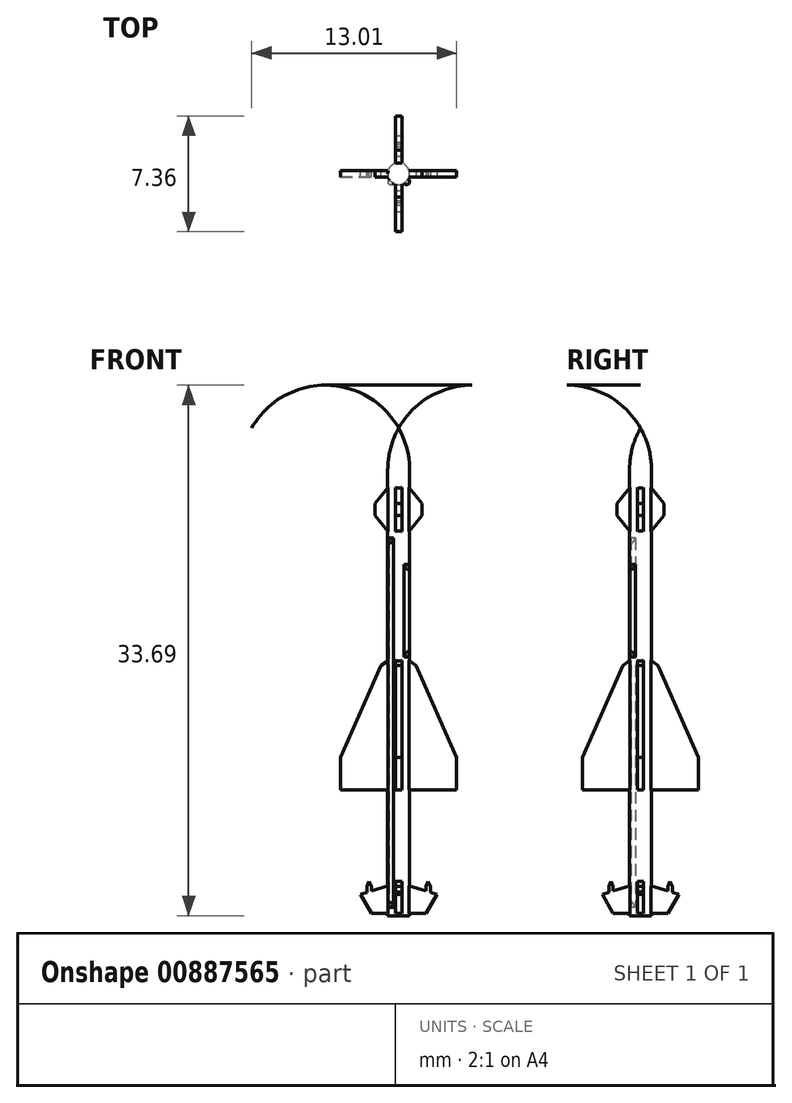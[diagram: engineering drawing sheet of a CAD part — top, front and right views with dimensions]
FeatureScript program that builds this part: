
annotation { "Feature Type Name" : "Feature", "Feature Type Description" : "" }
export const myFeature = defineFeature(function(context is Context, id is Id, definition is map)
    precondition{}
    {
        {
            var Q0;
            Q0=qCreatedBy(makeId("Front.planeOp"),FACE);
            var sketch = newSketch(context, id + "F0", { "sketchPlane" : qUnion([Q0])});
            skLineSegment(sketch, "E0", {"start": v(0, 0) * mm, "end": v(0, 30.97) * mm});
            skLineSegment(sketch, "E1", {"start": v(0.7, 28.33) * mm, "end": v(0.7, 0) * mm});
            skLineSegment(sketch, "E2", {"start": v(0.7, 0) * mm, "end": v(0, 0) * mm});
            skArc(sketch, "E3", {"start": v(0.7, 28.33) * mm, "mid": v(0.52, 29.7) * mm, "end": v(0, 30.97) * mm});
            skSolve(sketch);
        }
        {
            var Q0;
            Q0=makeQuery(id+"F0.imprint","IMPRINT",FACE,{"disambiguationData":[TD([[makeQuery(id+"F0.imprint","IMPRINT",EDGE,{"derivedFrom":sQuery(id+"F0.wireOp",EDGE,"E0")}),-1.0]])]});
            var Q1;
            Q1=sQuery(id+"F0.wireOp",EDGE,"E0");
            revolve(context, id + "F1", {"surfaceOperationType" : NewSurfaceOperationType.NEW, "entities" : qUnion([Q0]), "axis" : qUnion([Q1]), "revolveType" : RevolveType.FULL});
        }
        {
            var Q0;
            Q0=qCreatedBy(makeId("Front.planeOp"),FACE);
            var sketch = newSketch(context, id + "F2", { "sketchPlane" : qUnion([Q0])});
            skLineSegment(sketch, "E4.0", {"start": v(0.7, 28.33) * mm, "end": v(-0.7, 28.33) * mm, "construction": true});
            skLineSegment(sketch, "E5", {"start": v(0, 0.14) * mm, "end": v(1.74, 0.14) * mm});
            skLineSegment(sketch, "E6", {"start": v(2.43, 1.35) * mm, "end": v(0.7, 1.87) * mm});
            skLineSegment(sketch, "E7", {"start": v(0.4, 1.96) * mm, "end": v(0.4, 7.99) * mm});
            skLineSegment(sketch, "E8", {"start": v(0.4, 7.99) * mm, "end": v(3.68, 7.99) * mm});
            skLineSegment(sketch, "E9", {"start": v(0, 28) * mm, "end": v(0, 0.14) * mm});
            skLineSegment(sketch, "E10", {"start": v(0.7, 28.33) * mm, "end": v(0.7, 0) * mm, "construction": true});
            skLineSegment(sketch, "E11", {"start": v(0.7, 1.88) * mm, "end": v(0.4, 1.96) * mm});
            skLineSegment(sketch, "E12", {"start": v(1.74, 0.14) * mm, "end": v(2.43, 1.35) * mm});
            skLineSegment(sketch, "E13", {"start": v(3.68, 7.99) * mm, "end": v(3.68, 10.03) * mm});
            skLineSegment(sketch, "E14", {"start": v(0.4, 16.38) * mm, "end": v(0.4, 24.09) * mm});
            skLineSegment(sketch, "E15", {"start": v(1.5, 25.42) * mm, "end": v(0.4, 24.09) * mm});
            skLineSegment(sketch, "E16", {"start": v(1.5, 25.42) * mm, "end": v(1.5, 26.18) * mm});
            skLineSegment(sketch, "E17", {"start": v(1.5, 26.18) * mm, "end": v(0, 28) * mm});
            skLineSegment(sketch, "E18", {"start": v(1.74, 1.56) * mm, "end": v(1.74, 1.85) * mm});
            skLineSegment(sketch, "E19", {"start": v(1.74, 1.85) * mm, "end": v(1.87, 2.19) * mm});
            skLineSegment(sketch, "E20", {"start": v(1.87, 2.19) * mm, "end": v(2.01, 1.85) * mm});
            skLineSegment(sketch, "E21", {"start": v(2.01, 1.85) * mm, "end": v(2.01, 1.48) * mm});
            skLineSegment(sketch, "E22", {"start": v(3.68, 10.03) * mm, "end": v(1.11, 15.9) * mm});
            skLineSegment(sketch, "E23", {"start": v(1.11, 15.9) * mm, "end": v(0.4, 16.38) * mm});
            skPoint(sketch, "E24", {"position": v(0.7, 16.18) * mm});
            skPoint(sketch, "E25", {"position": v(0.7, 24.44) * mm});
            skPoint(sketch, "E26", {"position": v(0.7, 27.15) * mm});
            skSolve(sketch);
        }
        {
            var Q0;
            Q0=qSketchRegion(id+"F2",true);
            extrude(context, id + "F3", {"entities" : qUnion([Q0]), "operationType" : NewBodyOperationType.ADD, "oppositeDirection" : true, "depth" : .4 * mm, "offsetDistance" : 25 * mm, "symmetric" : true});
        }
        {
            var Q0;
            Q0=makeQuery(id+"F1.opRevolve","SWEPT_BODY",BODY,{"disambiguationData":[OSD([sQuery(id+"F0.wireOp",EDGE,"E0"),sQuery(id+"F0.wireOp",EDGE,"E1"),sQuery(id+"F0.wireOp",EDGE,"E2"),sQuery(id+"F0.wireOp",EDGE,"h1jDSi8t-veb7-85qg-XgDk-6E8DmZjBuz4r")])]});
            var Q1;
            Q1=makeQuery(id+"F1.opRevolve","SWEPT_FACE",FACE,{"disambiguationData":[OSD([sQuery(id+"F0.wireOp",EDGE,"E1")])]});
            circularPattern(context, id + "F4", {"operationType" : NewBodyOperationType.ADD, "entities" : qUnion([Q0]), "axis" : qUnion([Q1]), "angle" : 360 * degree, "instanceCount" : 4, "equalSpace" : true, "computeTransformsWithoutBuiltin" : true});
        }
        {
            var Q0;
            Q0=qCreatedBy(makeId("Top.planeOp"),FACE);
            cPlane(context, id + "F5", {"entities" : qUnion([Q0]), "cplaneType" : CPlaneType.OFFSET, "offset" : (140 / 144) * mm, "width" : 150 * mm, "height" : 150 * mm});
        }
        {
            var Q0;
            Q0=qCreatedBy(id+"F5.planeOp",FACE);
            var sketch = newSketch(context, id + "F6", { "sketchPlane" : qUnion([Q0])});
            skLineSegment(sketch, "E27", {"start": v(-0.63, -0.35) * mm, "end": v(-0.44, -0.15) * mm});
            skLineSegment(sketch, "E28", {"start": v(-0.44, -0.15) * mm, "end": v(-0.15, -0.44) * mm});
            skLineSegment(sketch, "E29", {"start": v(-0.15, -0.44) * mm, "end": v(-0.35, -0.63) * mm});
            skArc(sketch, "E30", {"start": v(-0.63, -0.35) * mm, "mid": v(-0.63, -0.63) * mm, "end": v(-0.35, -0.63) * mm});
            skLineSegment(sketch, "E31", {"start": v(-0.3, -0.3) * mm, "end": v(0, 0) * mm, "construction": true});
            skLineSegment(sketch, "E32", {"start": v(0, 0) * mm, "end": v(-0.48, 0) * mm, "construction": true});
            skSolve(sketch);
        }
        {
            var Q0;
            Q0=makeQuery(id+"F6.imprint","IMPRINT",FACE,{"disambiguationData":[TD([[makeQuery(id+"F6.imprint","IMPRINT",EDGE,{"derivedFrom":sQuery(id+"F6.wireOp",EDGE,"E27")}),-1.0]])]});
            extrude(context, id + "F7", {"entities" : qUnion([Q0]), "operationType" : NewBodyOperationType.ADD, "depth" : (3250 / 144) * mm, "offsetDistance" : 25 * mm});
        }
        {
            var Q0;
            Q0=qCreatedBy(makeId("Top.planeOp"),FACE);
            cPlane(context, id + "F8", {"entities" : qUnion([Q0]), "cplaneType" : CPlaneType.OFFSET, "offset" : (2430 / 144) * mm, "width" : 150 * mm, "height" : 150 * mm});
        }
        {
            var Q0;
            Q0=qCreatedBy(id+"F8.planeOp",FACE);
            var sketch = newSketch(context, id + "F9", { "sketchPlane" : qUnion([Q0])});
            skLineSegment(sketch, "E33", {"start": v(-0.05, -0.24) * mm, "end": v(0.24, 0.05) * mm});
            skLineSegment(sketch, "E34", {"start": v(0.24, 0.05) * mm, "end": v(0.64, -0.35) * mm});
            skLineSegment(sketch, "E35", {"start": v(0.35, -0.64) * mm, "end": v(-0.05, -0.24) * mm});
            skArc(sketch, "E36", {"start": v(0.35, -0.64) * mm, "mid": v(0.64, -0.64) * mm, "end": v(0.64, -0.35) * mm});
            skLineSegment(sketch, "E37", {"start": v(0, -0.58) * mm, "end": v(0, 0) * mm, "construction": true});
            skLineSegment(sketch, "E38", {"start": v(0, 0) * mm, "end": v(0.1, -0.1) * mm, "construction": true});
            skSolve(sketch);
        }
        {
            var Q0;
            Q0=qSketchRegion(id+"F9",true);
            extrude(context, id + "F10", {"entities" : qUnion([Q0]), "operationType" : NewBodyOperationType.ADD, "depth" : (720 / 144) * mm, "offsetDistance" : 25 * mm});
        }
        {
            var Q0;
            Q0=makeQuery(id+"F7.boolean.opBoolean","INTERSECT",EDGE,{"derivedFrom":[makeQuery(id+"F1.opRevolve","SWEPT_FACE",FACE,{"disambiguationData":[OSD([sQuery(id+"F0.wireOp",EDGE,"E1")])]}),makeQuery(id+"F7.opExtrude","CAP_FACE",FACE,{"disambiguationData":[OSD([sQuery(id+"F6.wireOp",EDGE,"E27"),sQuery(id+"F6.wireOp",EDGE,"E28"),sQuery(id+"F6.wireOp",EDGE,"E29"),sQuery(id+"F6.wireOp",EDGE,"E30")])],"isStart":false})]});
            var Q1;
            Q1=makeQuery(id+"F7.boolean.opBoolean","INTERSECT",EDGE,{"derivedFrom":[makeQuery(id+"F1.opRevolve","SWEPT_FACE",FACE,{"disambiguationData":[OSD([sQuery(id+"F0.wireOp",EDGE,"E1")])]}),makeQuery(id+"F7.opExtrude","CAP_FACE",FACE,{"disambiguationData":[OSD([sQuery(id+"F6.wireOp",EDGE,"E27"),sQuery(id+"F6.wireOp",EDGE,"E28"),sQuery(id+"F6.wireOp",EDGE,"E29"),sQuery(id+"F6.wireOp",EDGE,"E30")])],"isStart":true})]});
            var Q2;
            Q2=makeQuery(id+"F10.boolean.opBoolean","INTERSECT",EDGE,{"derivedFrom":[makeQuery(id+"F1.opRevolve","SWEPT_FACE",FACE,{"disambiguationData":[OSD([sQuery(id+"F0.wireOp",EDGE,"E1")])]}),makeQuery(id+"F10.opExtrude","CAP_FACE",FACE,{"disambiguationData":[OSD([sQuery(id+"F9.wireOp",EDGE,"E33"),sQuery(id+"F9.wireOp",EDGE,"E34"),sQuery(id+"F9.wireOp",EDGE,"E35"),sQuery(id+"F9.wireOp",EDGE,"E36")])],"isStart":true})]});
            var Q3;
            Q3=makeQuery(id+"F10.boolean.opBoolean","INTERSECT",EDGE,{"derivedFrom":[makeQuery(id+"F1.opRevolve","SWEPT_FACE",FACE,{"disambiguationData":[OSD([sQuery(id+"F0.wireOp",EDGE,"E1")])]}),makeQuery(id+"F10.opExtrude","CAP_FACE",FACE,{"disambiguationData":[OSD([sQuery(id+"F9.wireOp",EDGE,"E33"),sQuery(id+"F9.wireOp",EDGE,"E34"),sQuery(id+"F9.wireOp",EDGE,"E35"),sQuery(id+"F9.wireOp",EDGE,"E36")])],"isStart":false})]});
            chamfer(context, id + "F11", {"entities" : qUnion([Q0, Q1, Q2, Q3]), "chamferType" : ChamferType.OFFSET_ANGLE, "width" : .25 * mm, "oppositeDirection" : true, "angle" : 60 * degree, "tangentPropagation" : true});
        }
    });
